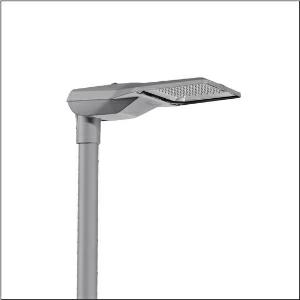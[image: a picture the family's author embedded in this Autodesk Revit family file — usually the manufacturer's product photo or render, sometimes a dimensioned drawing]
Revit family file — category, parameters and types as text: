
# Revit family: streetlight_sl_21_iq_midi___st1_0ab_5xe3m31v08mb_24a1
name_source: partatom
category: Lighting Fixtures
units: mm (PartAtom-declared; Revit-internal decimal feet)

## family parameters
Cut with Voids When Loaded = No
Host = Face
Light Source = No
Part Type = Normal
Room Calculation Point = No
Round Connector Dimension = Use Diameter
Shared = No

## types (1)
- --- (1 x LED, 16140 lm, 129.3 W, 3000K)
    Apparent Load = 129 VA
    CIE Flux Codes = 38 73 97 100 100
    Color Rendering = 70
    Color Temperature = 3000K
    Default Elevation = 1800 mm
    Description = Streetlight SL 21 iQ midi, mast luminaire, primary light control with lens, of PMMA, primary optical cover: cover, of toughened safety glass, transparent, light distribution: ST1.0aB, light emission: direct distribution, primary light characteristic: asymmetric, installation type: post-top, side-entry, LED, High Power LED, rated luminous flux: 16.140lm, luminous efficacy: 125lm/W, light colour: 730, colour temperature: 3000K, control: presetting dimming logarithmic, Street-Remote, Auto-Match, Temp-Guard, Lumen-Switch, Night-Set, Smart-Wire, Light-Fading, Desk-Remote (wireless, voltage-free reading and setting of iQ features in the workshop via application-optimized NFC function/RFID function), optimised constant luminous flux control (CLO 2.0), mains connection: 230..240V, AC, 50/60Hz, start of lifetime: 129W, end of service life: 142W, reduction: 56W, luminaire housing, of diecast aluminium, powder-coated, Siteco® metallic grey (DB 702S), corrosivity category C5 mid according to DIN EN ISO 12944, please order mast flange separately, inclination adjustable: 0°, 5°, 10°, 15°, sealing non-destructively replaceable, multi-level sealing system, length: 644mm, width: 335mm, height: 110mm, mast flange for spigot size: 42mm (side-entry): 5XC10008XM4, 60/48mm (side-entry/post-top): 5XC10108XM2, 76/60mm (side-entry/post-top): 5XC10108XM1, Smart Interface above, protection rating (complete): IP66, insulation class (complete): insulation class II (safety insulation), certification: CE, ENEC, ENEC+, VDE, impact resistance: IK09, permissible operating ambient temperature for outdoor applications: -40..+50°C, standard-compliant lighting for roads and squares, packaging unit: 1 piece

Light Distribution: ST1.0aB
    Height = 111 mm
    Lamp = 1 x LED
    Lamp Light Flux = 16140 lm
    Lamp Power = 129.3 W
    Lamp count = 1
    Length = 644 mm
    Luminous efficacy = 125 lm/W
    Manufacturer = Siteco
    ModVariant = No
    Model = 5XE3M31V08MB
    Number of Poles = 1
    OnlyDefault = Yes
    Power Factor = 1
    Product Name = Streetlight SL 21 iQ midi | ST1.0aB
    Product group = mast luminaire | pylon top
    ProductGroupID = 6100
    Protection Class = Protection class II
    Protection Degree = IP 66
    RLX_Detail_Level = 1
    RLX_Emergency_Light_Flux = 0 lm
    RLX_Emergency_Type = 0
    RLX_Emergency_Type_DB = No
    RlxData = <blob elided: 90821 chars, md5=5d1c2afe>
    Socket = socket
    Standby Power = 0 W
    System Light Flux = 16141 lm
    System Power = 129 W
    Type Comments = factory setting: luminous flux: 100 % | dim-lin: 254 | 672 mA
    Type Image = l_1004302.jpg
    URL = http://relux.com
    VarID = @adj_042407
    Voltage = 0 V
    Weight = 0.00 kg
    Width = 336 mm

## geometry (parser evidence)
native form markers: Blend x4, Sweep x12
no freeform markers — native parametric forms only
